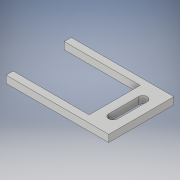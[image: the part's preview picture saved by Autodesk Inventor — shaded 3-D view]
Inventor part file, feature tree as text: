
AUTODESK INVENTOR PART (.ipt)
format: ipt  version: 2017 (Build 210142000, 142)  size: 112,128 bytes
history: native  units: mm
features: other x1, extrude x1, sketch x1
ambient origin geometry x8: Origin, YZ Plane, XZ Plane, XY Plane, X Axis, Y Axis, Z Axis, Center Point
bodies: Body1 (feature_tree)
feature tree (3):
  other  "Твердое тело1"
  extrude  "Выдавливание1"  Depth=9.0mm
  sketch  "Эскиз1"
